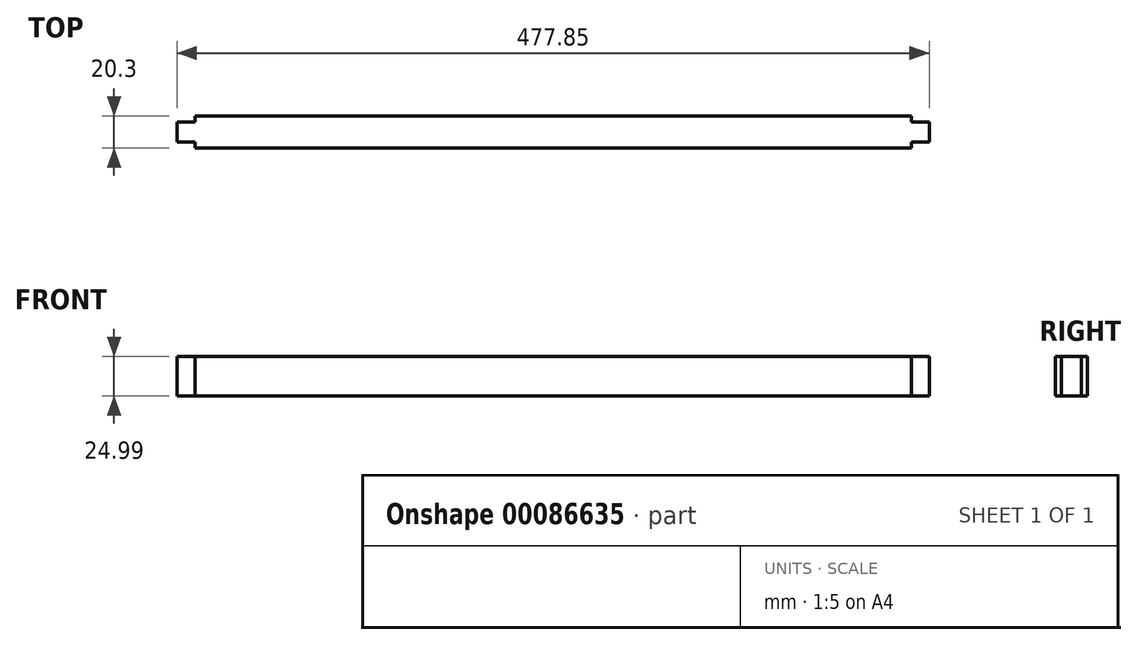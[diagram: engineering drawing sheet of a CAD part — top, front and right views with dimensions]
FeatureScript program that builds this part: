
annotation { "Feature Type Name" : "Feature", "Feature Type Description" : "" }
export const myFeature = defineFeature(function(context is Context, id is Id, definition is map)
    precondition{}
    {
        {
            var Q0;
            Q0=qCreatedBy(makeId("Top.planeOp"),FACE);
            var sketch = newSketch(context, id + "F0", { "sketchPlane" : qUnion([Q0])});
            skLineSegment(sketch, "E0.bottom", {"start": v(182.25, 3.91) * mm, "end": v(-272.74, 3.91) * mm});
            skLineSegment(sketch, "E0.top", {"start": v(182.25, 24.2) * mm, "end": v(-272.74, 24.2) * mm});
            skLineSegment(sketch, "E0.left", {"start": v(182.25, 3.91) * mm, "end": v(182.25, 7.7) * mm});
            skLineSegment(sketch, "E0.right", {"start": v(-272.74, 3.91) * mm, "end": v(-272.74, 7.7) * mm});
            skPoint(sketch, "E0.middle", {"position": v(-45.25, 14.06) * mm});
            skLineSegment(sketch, "E1.bottom", {"start": v(-272.74, 7.7) * mm, "end": v(-284.17, 7.7) * mm});
            skLineSegment(sketch, "E1.top", {"start": v(-272.74, 20.4) * mm, "end": v(-284.17, 20.4) * mm});
            skLineSegment(sketch, "E1.right", {"start": v(-284.17, 7.7) * mm, "end": v(-284.17, 20.4) * mm});
            skPoint(sketch, "E1.middle", {"position": v(-272.74, 14.06) * mm});
            skLineSegment(sketch, "E2.bottom", {"start": v(193.68, 7.7) * mm, "end": v(182.25, 7.7) * mm});
            skLineSegment(sketch, "E2.top", {"start": v(193.68, 20.4) * mm, "end": v(182.25, 20.4) * mm});
            skLineSegment(sketch, "E2.left", {"start": v(193.68, 7.7) * mm, "end": v(193.68, 20.4) * mm});
            skPoint(sketch, "E2.middle", {"position": v(182.25, 14.06) * mm});
            skPoint(sketch, "E1.left.end.orphan", {"position": v(-261.31, 20.4) * mm});
            skPoint(sketch, "E3.orphan", {"position": v(-261.31, 7.7) * mm});
            skLineSegment(sketch, "E4.trimOffspring", {"start": v(-272.74, 20.4) * mm, "end": v(-272.74, 24.2) * mm});
            skPoint(sketch, "E2.right.end.orphan", {"position": v(170.82, 20.4) * mm});
            skPoint(sketch, "E5.orphan", {"position": v(170.82, 7.7) * mm});
            skLineSegment(sketch, "E6.trimOffspring", {"start": v(182.25, 20.4) * mm, "end": v(182.25, 24.2) * mm});
            skSolve(sketch);
        }
        {
            var Q0;
            Q0 = qSketchRegion(id + "F0", true);
            extrude(context, id + "F1", {"entities" : qUnion([Q0]), "depth" : 25 * mm});
        }
    });
